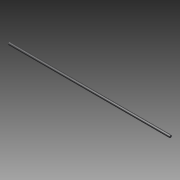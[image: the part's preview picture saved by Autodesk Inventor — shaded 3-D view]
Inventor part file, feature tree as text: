
AUTODESK INVENTOR PART (.ipt)
format: ipt  version: 2011 SP1 (Build 150282100, 282)  size: 92,672 bytes
history: native  units: mm
features: other x7, revolve x3, sketch x3, thread x1
ambient origin geometry x8: Origin, YZ Plane, XZ Plane, XY Plane, X Axis, Y Axis, Z Axis, Center Point
bodies: Solid1 (feature_tree)
feature tree (14):
  revolve  "Revolution1"  [1 undecoded]
  thread  "Thread1"  [1 undecoded]
  revolve  "Revolution2"  [1 undecoded]
  revolve  "Revolution3"  [1 undecoded]
  other  "bnt_s_1_XY"
  other  "bnt_s_1_YZ"
  other  "bnt_s_1_ZX"
  other  "bnt_s_1_X"
  other  "bnt_s_1_Y"
  other  "bnt_s_1_Z"
  other  "bnt_s_1_Center"
  sketch  "Sketch_1"  dims[d0=360.0deg d1=1258.0mm d2=0.0mm d3=360.0deg]
  sketch  "Sketch_2"  dims[d4=360.0deg d5=0.0mm]
  sketch  "Sketch_3"
note: 4 required parameter values undecoded (feature->parameter linkage not recoverable at this tier; creation-order binding heuristic only, values carry confidence <= 0.55)